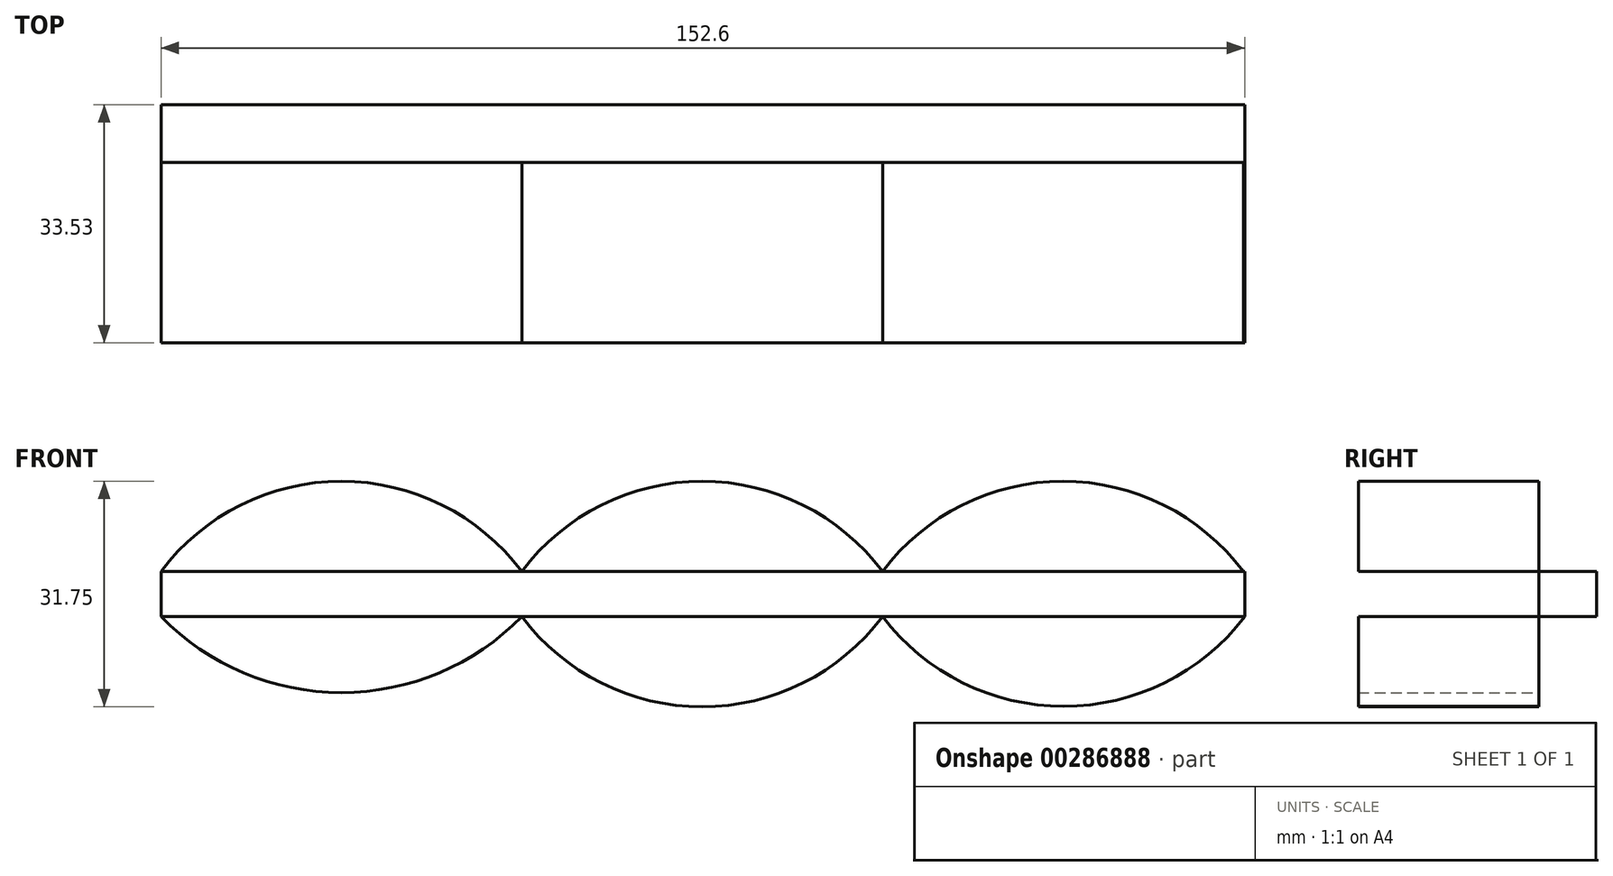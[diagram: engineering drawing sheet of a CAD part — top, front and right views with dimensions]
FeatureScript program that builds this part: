
annotation { "Feature Type Name" : "Feature", "Feature Type Description" : "" }
export const myFeature = defineFeature(function(context is Context, id is Id, definition is map)
    precondition{}
    {
        {
            var Q0;
            Q0=qCreatedBy(makeId("Front.planeOp"),FACE);
            var sketch = newSketch(context, id + "F0", { "sketchPlane" : qUnion([Q0])});
            skArc(sketch, "E0", {"start": v(-21.97, 0) * mm, "mid": v(-47.37, 12.7) * mm, "end": v(-72.77, 0) * mm});
            skArc(sketch, "E1", {"start": v(28.83, 0) * mm, "mid": v(3.43, 12.7) * mm, "end": v(-21.97, 0) * mm});
            skArc(sketch, "E2", {"start": v(79.63, 0) * mm, "mid": v(54.23, 12.7) * mm, "end": v(28.83, 0) * mm});
            skLineSegment(sketch, "E3.bottom", {"start": v(-72.77, 0) * mm, "end": v(79.83, 0) * mm});
            skLineSegment(sketch, "E3.top", {"start": v(-72.77, -6.35) * mm, "end": v(79.83, -6.35) * mm});
            skLineSegment(sketch, "E3.left", {"start": v(-72.77, 0) * mm, "end": v(-72.77, -6.35) * mm});
            skLineSegment(sketch, "E3.right", {"start": v(79.83, 0) * mm, "end": v(79.83, -6.35) * mm});
            skArc(sketch, "E4", {"start": v(-72.77, -6.35) * mm, "mid": v(-47.37, -17.05) * mm, "end": v(-21.97, -6.35) * mm});
            skArc(sketch, "E5", {"start": v(-21.97, -6.35) * mm, "mid": v(3.43, -19.05) * mm, "end": v(28.83, -6.35) * mm});
            skArc(sketch, "E6", {"start": v(28.83, -6.35) * mm, "mid": v(54.33, -18.99) * mm, "end": v(79.83, -6.35) * mm});
            skSolve(sketch);
        }
        {
            var Q0;
            {var subQ0=sQuery(id+"F0.wireOp",EDGE,"E4");Q0=makeQuery(id+"F0.imprint","IMPRINT",FACE,{"disambiguationData":[TD([[makeQuery(id+"F0.imprint","IMPRINT",EDGE,{"derivedFrom":subQ0}),1.0]])]});}
            var Q1;
            {var subQ0=sQuery(id+"F0.wireOp",EDGE,"E0");Q1=makeQuery(id+"F0.imprint","IMPRINT",FACE,{"disambiguationData":[TD([[makeQuery(id+"F0.imprint","IMPRINT",EDGE,{"derivedFrom":subQ0}),1.0]])]});}
            var Q2;
            {var subQ0=sQuery(id+"F0.wireOp",EDGE,"E5");Q2=makeQuery(id+"F0.imprint","IMPRINT",FACE,{"disambiguationData":[TD([[makeQuery(id+"F0.imprint","IMPRINT",EDGE,{"derivedFrom":subQ0}),1.0]])]});}
            var Q3;
            {var subQ0=sQuery(id+"F0.wireOp",EDGE,"E1");Q3=makeQuery(id+"F0.imprint","IMPRINT",FACE,{"disambiguationData":[TD([[makeQuery(id+"F0.imprint","IMPRINT",EDGE,{"derivedFrom":subQ0}),1.0]])]});}
            var Q4;
            {var subQ0=sQuery(id+"F0.wireOp",EDGE,"E6");Q4=makeQuery(id+"F0.imprint","IMPRINT",FACE,{"disambiguationData":[TD([[makeQuery(id+"F0.imprint","IMPRINT",EDGE,{"derivedFrom":subQ0}),1.0]])]});}
            var Q5;
            {var subQ0=sQuery(id+"F0.wireOp",EDGE,"E2");Q5=makeQuery(id+"F0.imprint","IMPRINT",FACE,{"disambiguationData":[TD([[makeQuery(id+"F0.imprint","IMPRINT",EDGE,{"derivedFrom":subQ0}),1.0]])]});}
            extrude(context, id + "F1", {"entities" : qUnion([Q0, Q1, Q2, Q3, Q4, Q5]), "depth" : 25.4 * mm});
        }
        {
            var Q0;
            {var subQ8=sQuery(id+"F0.wireOp",EDGE,"E3.left");Q0=makeQuery(id+"F0.imprint","IMPRINT",FACE,{"disambiguationData":[TD([[makeQuery(id+"F0.imprint","IMPRINT",EDGE,{"derivedFrom":subQ8}),1.0]])]});}
            extrude(context, id + "F2", {"entities" : qUnion([Q0]), "oppositeDirection" : true, "depth" : 8.13 * mm});
        }
    });
